FCSTD DOCUMENT  (FreeCAD 1.2R20251216 (Git shallow))
Label: lesson43
License: All rights reserved
objects: Sketcher::SketchObject×3, App::Point×1, PartDesign::Plane×1, PartDesign::Body×1
note: 8 computed .brp shape members not serialized (recipe doc carries the construction recipe); baked Part::Feature solids carry a one-line shape summary decoded from their .brp

FEATURE [App::Point] Origin001
  Role = Origin
FEATURE [Sketcher::SketchObject] Sketch
  ArcFitTolerance = 1e-06
  AttachmentSupport = -> [Origin]
  ExternalTypes = [0]
  FullyConstrained = false
  MakeInternals = false
  MapMode = 5
  sketch-geometry (4):
    g0: ArcOfCircle CenterX=-17.8658 CenterY=0 CenterZ=0 NormalX=0 NormalY=0 NormalZ=1 AngleXU=0 Radius=10 StartAngle=1.5708 EndAngle=4.71239
    g1: ArcOfCircle CenterX=17.8658 CenterY=0 CenterZ=0 NormalX=0 NormalY=0 NormalZ=1 AngleXU=0 Radius=10 StartAngle=4.71239 EndAngle=7.85398
    g2: LineSegment StartX=-17.8658 StartY=10 StartZ=0 EndX=17.8658 EndY=10 EndZ=0
    g3: LineSegment StartX=-17.8658 StartY=-10 StartZ=0 EndX=17.8658 EndY=-10 EndZ=0
  constraints (8):
    c: Tangent(g0,g2) = 1.5708
    c: Tangent(g0,g3) = -1.5708
    c: Tangent(g1,g2) = 1.5708
    c: Tangent(g1,g3) = -1.5708
    c: Equal(g0,g1)
    c: Radius(g0) = 10
    c: PointOnObject(g0,g-1)
    c: Symmetric(g0,g1,g-1)
FEATURE [Sketcher::SketchObject] Sketch001
  ArcFitTolerance = 1e-06
  AttachmentOffset = pos=(0,0,20) rot=(0,0,1;0rad)
  AttachmentSupport = -> [Sketch]
  ExternalTypes = [0]
  FullyConstrained = false
  MakeInternals = false
  MapMode = 2
  Placement = pos=(0,0,20) rot=(0,0,1;0rad)
  sketch-geometry (4):
    g0: ArcOfCircle CenterX=-25.716 CenterY=0 CenterZ=0 NormalX=0 NormalY=0 NormalZ=1 AngleXU=0 Radius=20 StartAngle=1.5708 EndAngle=4.71239
    g1: ArcOfCircle CenterX=24.284 CenterY=0 CenterZ=0 NormalX=0 NormalY=0 NormalZ=1 AngleXU=0 Radius=20 StartAngle=4.71239 EndAngle=7.85398
    g2: LineSegment StartX=-25.716 StartY=20 StartZ=0 EndX=24.284 EndY=20 EndZ=0
    g3: LineSegment StartX=-25.716 StartY=-20 StartZ=0 EndX=24.284 EndY=-20 EndZ=0
  constraints (9):
    c: Tangent(g0,g2) = 1.5708
    c: Tangent(g0,g3) = -1.5708
    c: Tangent(g1,g2) = 1.5708
    c: Tangent(g1,g3) = -1.5708
    c: Equal(g0,g1)
    c: Radius(g0) = 20
    c: PointOnObject(g0,g-1)
    c: PointOnObject(g1,g-1)
    c: DistanceX(g2,g2) = 50
FEATURE [PartDesign::Plane] DatumPlane
  AttachmentOffset = pos=(0,0,45) rot=(0,0,1;0rad)
  AttachmentSupport = -> [XY_Plane]
  Length = 103.4
  MapMode = 5
  Placement = pos=(0,0,45) rot=(0,0,1;0rad)
  ResizeMode = 0
  Width = 63.4153
FEATURE [Sketcher::SketchObject] Sketch002
  ArcFitTolerance = 1e-06
  AttachmentSupport = -> [DatumPlane]
  ExternalTypes = [0]
  FullyConstrained = false
  MakeInternals = false
  MapMode = 5
  Placement = pos=(0,0,40) rot=(0,0,1;0rad)
  sketch-geometry (4):
    g0: ArcOfCircle CenterX=-43.8182 CenterY=0 CenterZ=0 NormalX=0 NormalY=0 NormalZ=1 AngleXU=0 Radius=47.7111 StartAngle=1.5708 EndAngle=4.71239
    g1: ArcOfCircle CenterX=40.8441 CenterY=0 CenterZ=0 NormalX=0 NormalY=0 NormalZ=1 AngleXU=0 Radius=47.7111 StartAngle=4.71239 EndAngle=7.85398
    g2: LineSegment StartX=-43.8182 StartY=47.7111 StartZ=0 EndX=40.8441 EndY=47.7111 EndZ=0
    g3: LineSegment StartX=-43.8182 StartY=-47.7111 StartZ=0 EndX=40.8441 EndY=-47.7111 EndZ=0
  constraints (7):
    c: Tangent(g0,g2) = 1.5708
    c: Tangent(g0,g3) = -1.5708
    c: Tangent(g1,g2) = 1.5708
    c: Tangent(g1,g3) = -1.5708
    c: Equal(g0,g1)
    c: PointOnObject(g0,g-1)
    c: PointOnObject(g1,g-1)
FEATURE [PartDesign::Body] Body
  AllowCompound = true
  Group = -> [Sketch,Sketch002,Sketch001,DatumPlane]
  Origin = -> Origin
